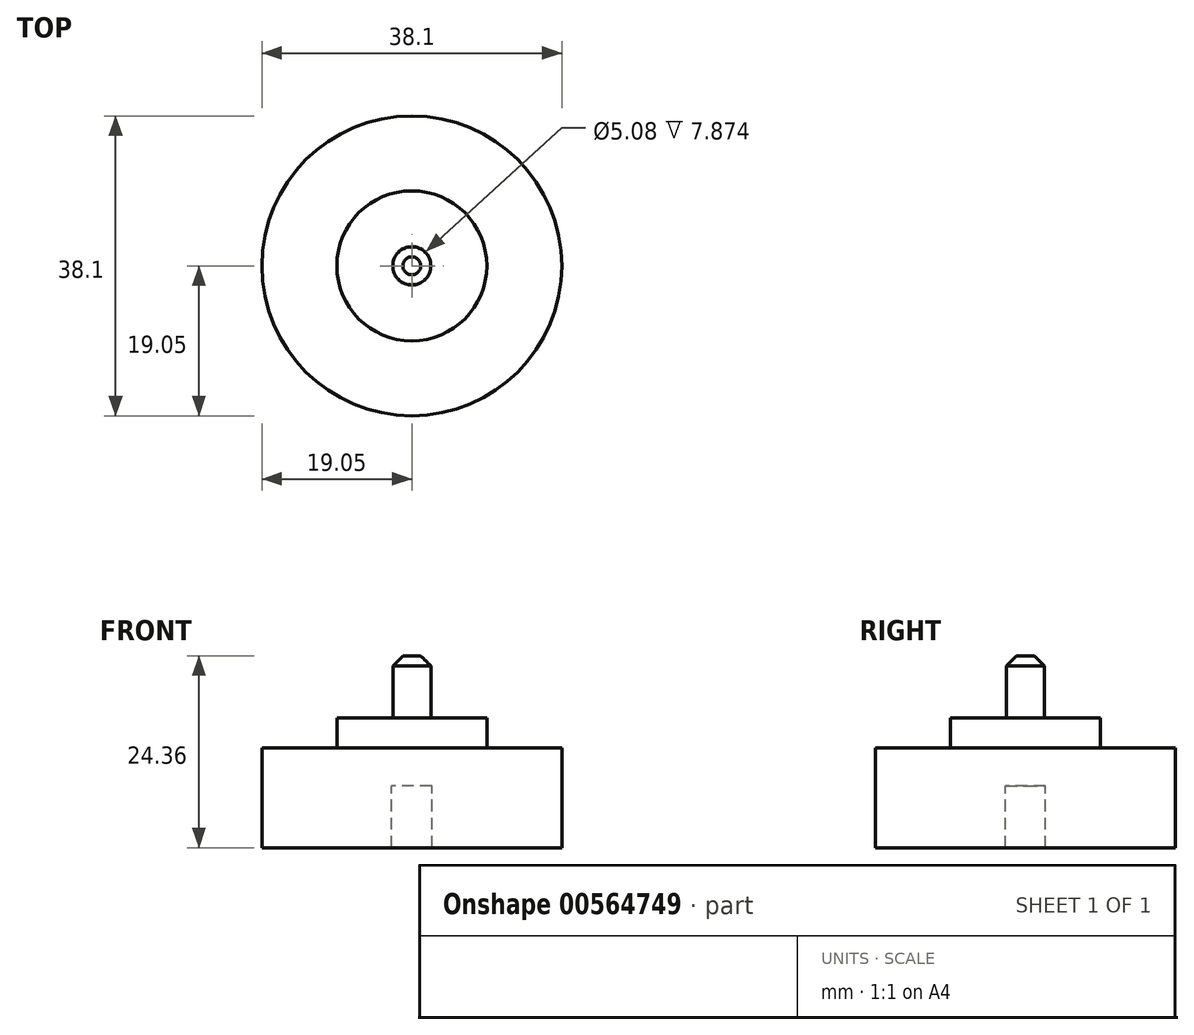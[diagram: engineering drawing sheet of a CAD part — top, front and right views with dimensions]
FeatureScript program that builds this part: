
annotation { "Feature Type Name" : "Feature", "Feature Type Description" : "" }
export const myFeature = defineFeature(function(context is Context, id is Id, definition is map)
    precondition{}
    {
        {
            var Q0;
            Q0=qCreatedBy(makeId("Front.planeOp"),FACE);
            var sketch = newSketch(context, id + "F0", { "sketchPlane" : qUnion([Q0])});
            skLineSegment(sketch, "E0", {"start": v(19.05, 0) * mm, "end": v(19.05, 12.7) * mm});
            skLineSegment(sketch, "E1", {"start": v(19.05, 12.7) * mm, "end": v(9.53, 12.7) * mm});
            skLineSegment(sketch, "E2", {"start": v(2.41, 16.51) * mm, "end": v(9.53, 16.51) * mm});
            skPoint(sketch, "E2.endSnap0", {"position": v(9.53, 12.7) * mm});
            skLineSegment(sketch, "E3", {"start": v(2.54, 0) * mm, "end": v(2.54, 7.87) * mm});
            skLineSegment(sketch, "E4", {"start": v(2.54, 7.87) * mm, "end": v(0, 7.87) * mm});
            skLineSegment(sketch, "E5", {"start": v(0, 24.36) * mm, "end": v(2.41, 24.36) * mm});
            skLineSegment(sketch, "E6", {"start": v(2.41, 24.36) * mm, "end": v(2.41, 16.51) * mm});
            skLineSegment(sketch, "E7", {"start": v(9.53, 16.51) * mm, "end": v(9.53, 12.7) * mm});
            skLineSegment(sketch, "E8", {"start": v(2.54, 0) * mm, "end": v(19.05, 0) * mm});
            skLineSegment(sketch, "E9", {"start": v(0, 24.36) * mm, "end": v(0, 7.87) * mm});
            skSolve(sketch);
        }
        {
            var Q0;
            Q0 = qSketchRegion(id + "F0", true);
            var Q1;
            Q1=sQuery(id+"F0.wireOp",EDGE,"E9");
            revolve(context, id + "F1", {"entities" : qUnion([Q0]), "axis" : qUnion([Q1]), "revolveType" : RevolveType.FULL});
        }
        {
            var Q0;
            Q0=makeQuery(id+"F1.opRevolve","SWEPT_EDGE",EDGE,{"disambiguationData":[OSD([sQuery(id+"F0.wireOp",EDGE,"E5"),sQuery(id+"F0.wireOp",EDGE,"E6")])]});
            chamfer(context, id + "F2", {"entities" : qUnion([Q0]), "width" : 1.27 * mm, "tangentPropagation" : true});
        }
    });
